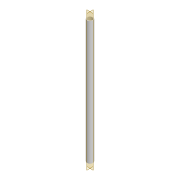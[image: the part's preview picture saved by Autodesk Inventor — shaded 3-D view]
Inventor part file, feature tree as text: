
AUTODESK INVENTOR PART (.ipt)
format: ipt  version: 2022 (Build 260153000, 153)  size: 77,824 bytes
history: native  units: mm
features: extrude x1, sketch x1
ambient origin geometry x8: Origin, YZ Plane, XZ Plane, XY Plane, X Axis, Y Axis, Z Axis, Center Point
bodies: Body1 (feature_tree)
feature tree (2):
  extrude  "Extrusion2"  Depth=250.0mm
  sketch  "Sketch2"  dims[d6=10.0mm d7=12.0mm d8=250.0mm d9=0.0mm]
